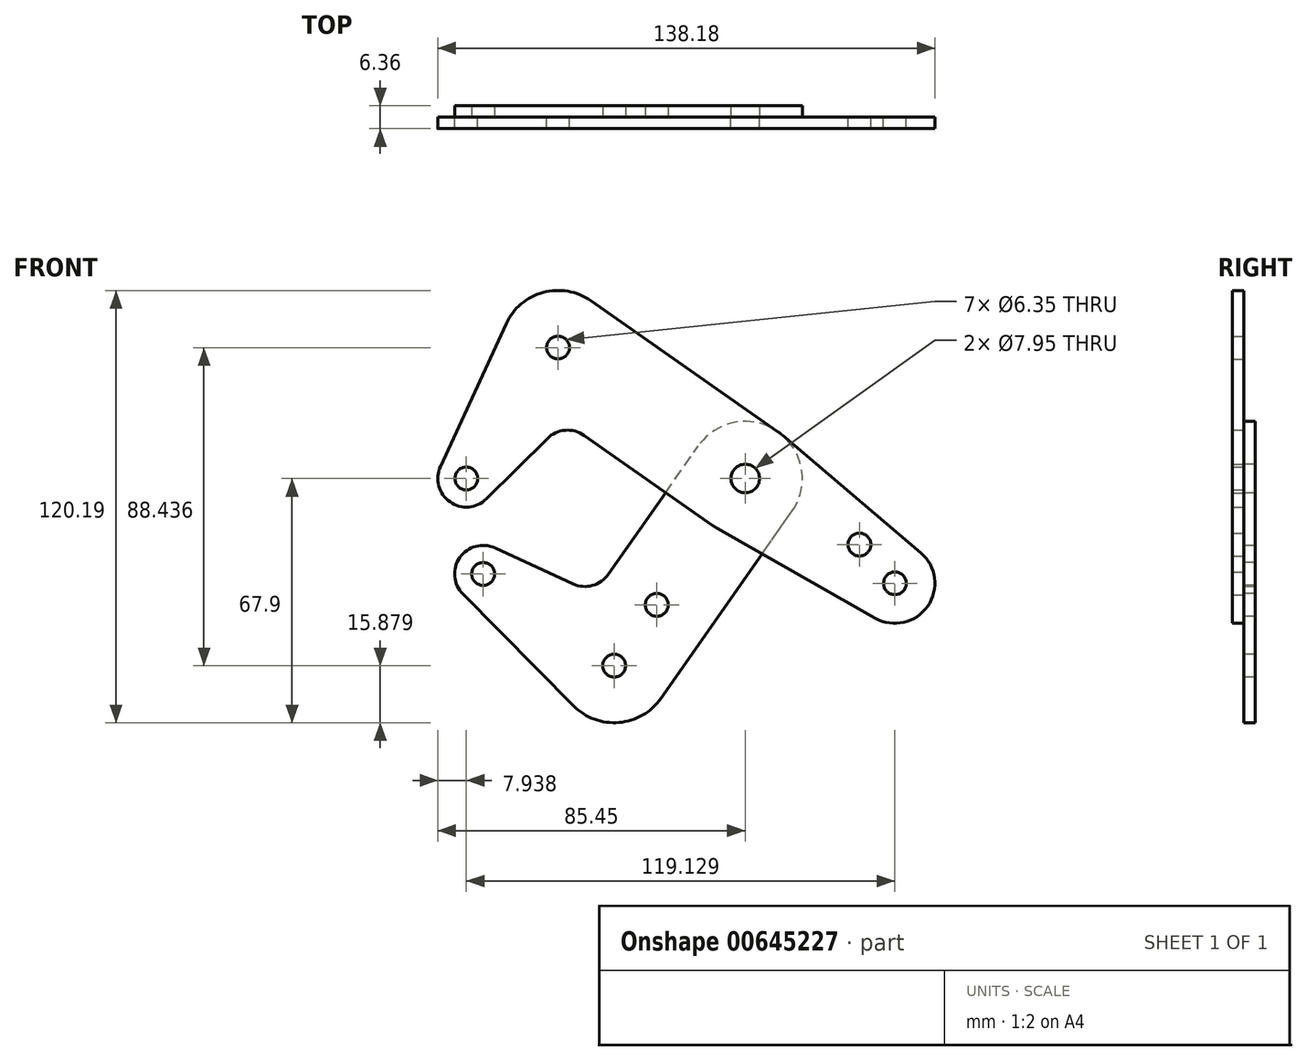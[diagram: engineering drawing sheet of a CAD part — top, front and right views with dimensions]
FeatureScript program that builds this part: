
annotation { "Feature Type Name" : "Feature", "Feature Type Description" : "" }
export const myFeature = defineFeature(function(context is Context, id is Id, definition is map)
    precondition{}
    {
        {
            var Q0;
            Q0=qCreatedBy(makeId("Front.planeOp"),FACE);
            var sketch = newSketch(context, id + "F0", { "sketchPlane" : qUnion([Q0])});
            skLineSegment(sketch, "E0", {"start": v(0, 0) * mm, "end": v(-52.02, 36.41) * mm, "construction": true});
            skLineSegment(sketch, "E1", {"start": v(0, 0) * mm, "end": v(41.62, -29.13) * mm, "construction": true});
            skLineSegment(sketch, "E2", {"start": v(-52.02, 36.41) * mm, "end": v(-77.51, 0) * mm, "construction": true});
            skCircle(sketch, "E3", {"center": v(-77.51, 0) * mm, "radius": 7.94 * mm});
            skCircle(sketch, "E4", {"center": v(-52.02, 36.41) * mm, "radius": 15.88 * mm});
            skCircle(sketch, "E5", {"center": v(0, 0) * mm, "radius": 15.88 * mm});
            skCircle(sketch, "E6", {"center": v(41.62, -29.13) * mm, "radius": 11.11 * mm});
            skCircle(sketch, "E7", {"center": v(31.74, -18.34) * mm, "radius": 3.18 * mm});
            skLineSegment(sketch, "E8", {"start": v(0, 0) * mm, "end": v(9.14, 13.06) * mm, "construction": true});
            skCircle(sketch, "E9", {"center": v(41.62, -29.13) * mm, "radius": 3.18 * mm});
            skCircle(sketch, "E10", {"center": v(-77.51, 0) * mm, "radius": 3.18 * mm});
            skCircle(sketch, "E11", {"center": v(-52.02, 36.41) * mm, "radius": 3.18 * mm});
            skLineSegment(sketch, "E12", {"start": v(-84.72, 3.32) * mm, "end": v(-66.44, 43.05) * mm});
            skLineSegment(sketch, "E13", {"start": v(9.14, 13.06) * mm, "end": v(48.81, -20.67) * mm});
            skLineSegment(sketch, "E14", {"start": v(36.13, -38.8) * mm, "end": v(-7.84, -13.8) * mm});
            skLineSegment(sketch, "E15", {"start": v(-71.93, -5.64) * mm, "end": v(-54.98, 11.14) * mm});
            skLineSegment(sketch, "E16", {"start": v(-9.1, -13) * mm, "end": v(-44.83, 12) * mm});
            skArc(sketch, "E17.filletArc", {"start": v(-44.83, 12) * mm, "mid": v(-50.06, 13.41) * mm, "end": v(-54.98, 11.14) * mm});
            skCircle(sketch, "E18", {"center": v(0, 0) * mm, "radius": 3.98 * mm});
            skCircle(sketch, "E19", {"center": v(0, 0) * mm, "radius": 3.18 * mm});
            skLineSegment(sketch, "E20", {"start": v(0, 0) * mm, "end": v(-36.41, -52.02) * mm, "construction": true});
            skLineSegment(sketch, "E21", {"start": v(-36.41, -52.02) * mm, "end": v(-72.83, -26.53) * mm, "construction": true});
            skCircle(sketch, "E22", {"center": v(-36.41, -52.02) * mm, "radius": 15.88 * mm});
            skCircle(sketch, "E23", {"center": v(-24.57, -35.1) * mm, "radius": 3.17 * mm});
            skCircle(sketch, "E24", {"center": v(-72.83, -26.53) * mm, "radius": 7.94 * mm});
            skCircle(sketch, "E25", {"center": v(-72.83, -26.53) * mm, "radius": 3.18 * mm});
            skLineSegment(sketch, "E26", {"start": v(-23.4, -61.12) * mm, "end": v(13, -9.1) * mm});
            skLineSegment(sketch, "E27", {"start": v(-38.01, -26.62) * mm, "end": v(-13, 9.1) * mm});
            skLineSegment(sketch, "E28", {"start": v(-69.51, -19.32) * mm, "end": v(-47.85, -29.29) * mm});
            skArc(sketch, "E29.filletArc", {"start": v(-47.85, -29.29) * mm, "mid": v(-42.45, -29.74) * mm, "end": v(-38.01, -26.62) * mm});
            skCircle(sketch, "E30", {"center": v(-36.41, -52.02) * mm, "radius": 3.18 * mm});
            skLineSegment(sketch, "E31", {"start": v(-77.51, 0) * mm, "end": v(-72.83, -26.53) * mm, "construction": true});
            skLineSegment(sketch, "E32", {"start": v(-42.92, 49.42) * mm, "end": v(9.1, 13) * mm});
            skLineSegment(sketch, "E33", {"start": v(-78.47, -32.12) * mm, "end": v(-47.7, -63.2) * mm});
            skSolve(sketch);
        }
        {
            var Q0;
            {var subQ4=sQuery(id+"F0.wireOp",EDGE,"E12");Q0=makeQuery(id+"F0.imprint","IMPRINT",FACE,{"disambiguationData":[TD([[makeQuery(id+"F0.imprint","IMPRINT",EDGE,{"derivedFrom":subQ4}),-1.0]])]});}
            var Q1;
            Q1=makeQuery(id+"F0.imprint","IMPRINT",FACE,{"disambiguationData":[TD([[makeQuery(id+"F0.imprint","IMPRINT",EDGE,{"derivedFrom":sQuery(id+"F0.wireOp",EDGE,"E7")}),-1.0]])]});
            var Q2;
            Q2=makeQuery(id+"F0.imprint","IMPRINT",FACE,{"disambiguationData":[TD([[makeQuery(id+"F0.imprint","IMPRINT",EDGE,{"derivedFrom":sQuery(id+"F0.wireOp",EDGE,"E18")}),-1.0]])]});
            var Q3;
            {var subQ0=sQuery(id+"F0.wireOp",EDGE,"E14");var subQ1=sQuery(id+"F0.wireOp",EDGE,"E5");var subQ2=makeQuery(id+"F0.imprint","INTERSECT",VERTEX,{"derivedFrom":[subQ1,subQ0]});Q3=makeQuery(id+"F0.imprint","IMPRINT",FACE,{"disambiguationData":[TD([[makeQuery(id+"F0.imprint","IMPRINT",EDGE,{"disambiguationData":[TD([[subQ2,-1.0]])],"derivedFrom":subQ1}),-1.0]])]});}
            var Q4;
            {var subQ0=sQuery(id+"F0.wireOp",EDGE,"E16");var subQ1=sQuery(id+"F0.wireOp",EDGE,"E5");var subQ2=makeQuery(id+"F0.imprint","INTERSECT",VERTEX,{"derivedFrom":[subQ1,subQ0]});Q4=makeQuery(id+"F0.imprint","IMPRINT",FACE,{"disambiguationData":[TD([[makeQuery(id+"F0.imprint","IMPRINT",EDGE,{"disambiguationData":[TD([[subQ2,1.0]])],"derivedFrom":subQ1}),-1.0]])]});}
            var Q5;
            Q5=makeQuery(id+"F0.imprint","IMPRINT",FACE,{"disambiguationData":[TD([[makeQuery(id+"F0.imprint","IMPRINT",EDGE,{"derivedFrom":sQuery(id+"F0.wireOp",EDGE,"E11")}),-1.0]])]});
            var Q6;
            Q6=makeQuery(id+"F0.imprint","IMPRINT",FACE,{"disambiguationData":[TD([[makeQuery(id+"F0.imprint","IMPRINT",EDGE,{"derivedFrom":sQuery(id+"F0.wireOp",EDGE,"E10")}),-1.0]])]});
            var Q7;
            Q7=makeQuery(id+"F0.imprint","IMPRINT",FACE,{"disambiguationData":[TD([[makeQuery(id+"F0.imprint","IMPRINT",EDGE,{"derivedFrom":sQuery(id+"F0.wireOp",EDGE,"E9")}),-1.0]])]});
            extrude(context, id + "F1", {"entities" : qUnion([Q0, Q1, Q2, Q3, Q4, Q5, Q6, Q7]), "depth" : 3.17 * mm, "offsetDistance" : 25.4 * mm});
        }
        {
            var Q0;
            Q0=makeQuery(id+"F0.imprint","IMPRINT",FACE,{"disambiguationData":[TD([[makeQuery(id+"F0.imprint","IMPRINT",EDGE,{"derivedFrom":sQuery(id+"F0.wireOp",EDGE,"E23")}),-1.0]])]});
            var Q1;
            Q1=makeQuery(id+"F0.imprint","IMPRINT",FACE,{"disambiguationData":[TD([[makeQuery(id+"F0.imprint","IMPRINT",EDGE,{"derivedFrom":sQuery(id+"F0.wireOp",EDGE,"E30")}),-1.0]])]});
            var Q2;
            Q2=makeQuery(id+"F0.imprint","IMPRINT",FACE,{"disambiguationData":[TD([[makeQuery(id+"F0.imprint","IMPRINT",EDGE,{"derivedFrom":sQuery(id+"F0.wireOp",EDGE,"E25")}),-1.0]])]});
            var Q3;
            {var subQ0=sQuery(id+"F0.wireOp",EDGE,"E16");var subQ1=sQuery(id+"F0.wireOp",EDGE,"E5");var subQ2=makeQuery(id+"F0.imprint","INTERSECT",VERTEX,{"derivedFrom":[subQ1,subQ0]});Q3=makeQuery(id+"F0.imprint","IMPRINT",FACE,{"disambiguationData":[TD([[makeQuery(id+"F0.imprint","IMPRINT",EDGE,{"disambiguationData":[TD([[subQ2,1.0]])],"derivedFrom":subQ1}),-1.0]])]});}
            var Q4;
            {var subQ0=sQuery(id+"F0.wireOp",EDGE,"E14");var subQ1=sQuery(id+"F0.wireOp",EDGE,"E5");var subQ2=makeQuery(id+"F0.imprint","INTERSECT",VERTEX,{"derivedFrom":[subQ1,subQ0]});Q4=makeQuery(id+"F0.imprint","IMPRINT",FACE,{"disambiguationData":[TD([[makeQuery(id+"F0.imprint","IMPRINT",EDGE,{"disambiguationData":[TD([[subQ2,-1.0]])],"derivedFrom":subQ1}),-1.0]])]});}
            var Q5;
            Q5=makeQuery(id+"F0.imprint","IMPRINT",FACE,{"disambiguationData":[TD([[makeQuery(id+"F0.imprint","IMPRINT",EDGE,{"derivedFrom":sQuery(id+"F0.wireOp",EDGE,"E18")}),-1.0]])]});
            extrude(context, id + "F2", {"entities" : qUnion([Q0, Q1, Q2, Q3, Q4, Q5]), "oppositeDirection" : true, "depth" : 3.17 * mm, "offsetDistance" : 25.4 * mm});
        }
    });
